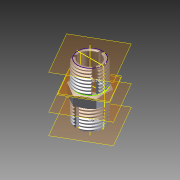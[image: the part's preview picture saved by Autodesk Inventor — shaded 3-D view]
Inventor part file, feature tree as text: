
AUTODESK INVENTOR PART (.ipt)
format: ipt  version: 2015 (Build 190159000, 159)  size: 4,501,504 bytes
history: native  units: in
note: dims shown in document units (in); Inventor stores cm internally (conversion verified against a paired STEP export)
features: sketch x5, plane x5, other x1, imported_body x1, projected_geometry x1
ambient origin geometry x8: Origin, YZ Plane, XZ Plane, XY Plane, X Axis, Y Axis, Z Axis, Center Point
bodies: Solid1 (feature_tree)
feature tree (13):
  other  "TaperedScrewCoupling_8x51"
  sketch  "Sketch1"  dims[d0=0.0197in]
  plane  "Work Plane1"
  plane  "Work Plane3"
  plane  "Work Plane5"
  sketch  "Sketch2"  dims[d1=0.2947in]
  sketch  "Sketch3"  dims[d2=0.0053in]
  sketch  "Sketch4"
  sketch  "Sketch5"
  imported_body  "Base1"
  plane  "Work Plane2"
  plane  "Work Plane4"
  projected_geometry  "Project Cut Edges1"
